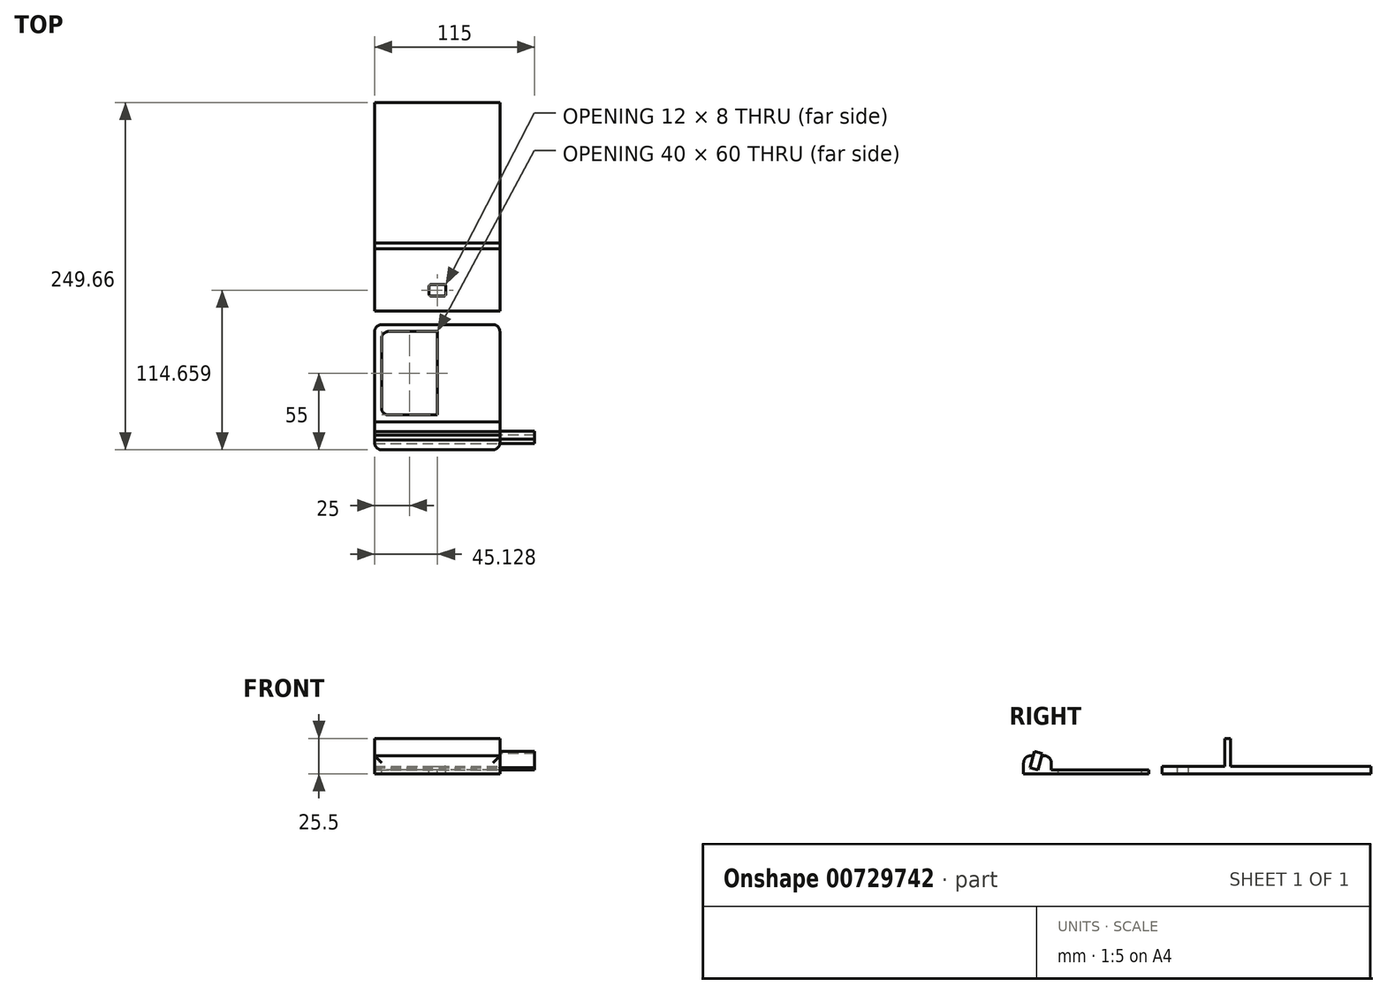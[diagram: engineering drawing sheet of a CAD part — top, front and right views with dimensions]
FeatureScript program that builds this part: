
annotation { "Feature Type Name" : "Feature", "Feature Type Description" : "" }
export const myFeature = defineFeature(function(context is Context, id is Id, definition is map)
    precondition{}
    {
        {
            var Q0;
            Q0=qCreatedBy(makeId("Top.planeOp"),FACE);
            var sketch = newSketch(context, id + "F0", { "sketchPlane" : qUnion([Q0])});
            skLineSegment(sketch, "E0.bottom", {"start": v(45, -45) * mm, "end": v(-45, -45) * mm});
            skLineSegment(sketch, "E0.top", {"start": v(45, 45) * mm, "end": v(-45, 45) * mm});
            skLineSegment(sketch, "E0.left", {"start": v(45, -45) * mm, "end": v(45, 45) * mm});
            skLineSegment(sketch, "E0.right", {"start": v(-45, -45) * mm, "end": v(-45, 45) * mm});
            skPoint(sketch, "E0.middle", {"position": v(0, 0) * mm});
            skSolve(sketch);
        }
        {
            var Q0;
            Q0 = qSketchRegion(id + "F0", true);
            extrude(context, id + "F1", {"entities" : qUnion([Q0]), "depth" : 3 * mm, "offsetDistance" : 25 * mm});
        }
        {
            var Q0;
            Q0=makeQuery(id+"F1.opExtrude","SWEPT_FACE",FACE,{"disambiguationData":[OSD([sQuery(id+"F0.wireOp",EDGE,"E0.left")])]});
            var sketch = newSketch(context, id + "F2", { "sketchPlane" : qUnion([Q0])});
            skLineSegment(sketch, "E1.bottom", {"start": v(-45, 3) * mm, "end": v(-25, 3) * mm});
            skLineSegment(sketch, "E1.top", {"start": v(-45, 13) * mm, "end": v(-25, 13) * mm});
            skLineSegment(sketch, "E1.left", {"start": v(-45, 3) * mm, "end": v(-45, 13) * mm});
            skLineSegment(sketch, "E1.right", {"start": v(-25, 3) * mm, "end": v(-25, 13) * mm});
            skSolve(sketch);
        }
        {
            var Q0;
            Q0=makeQuery(id+"F2.imprint","IMPRINT",FACE,{"disambiguationData":[TD([[makeQuery(id+"F2.imprint","IMPRINT",EDGE,{"derivedFrom":sQuery(id+"F2.wireOp",EDGE,"E1.bottom")}),1.0]])]});
            var Q1;
            Q1=makeQuery(id+"F1.opExtrude","SWEPT_FACE",FACE,{"disambiguationData":[OSD([sQuery(id+"F0.wireOp",EDGE,"E0.right")])]});
            extrude(context, id + "F3", {"entities" : qUnion([Q0]), "operationType" : NewBodyOperationType.ADD, "endBound" : BoundingType.UP_TO_SURFACE, "oppositeDirection" : true, "depth" : 25 * mm, "endBoundEntityFace" : qUnion([Q1]), "offsetDistance" : 25 * mm});
        }
        {
            var Q0;
            Q0=makeQuery(id+"F3.boolean.opBoolean","MERGE",FACE,{"derivedFrom":[makeQuery(id+"F1.opExtrude","SWEPT_FACE",FACE,{"disambiguationData":[OSD([sQuery(id+"F0.wireOp",EDGE,"E0.left")])]}),makeQuery(id+"F3.opExtrude","CAP_FACE",FACE,{"disambiguationData":[OSD([sQuery(id+"F2.wireOp",EDGE,"E1.bottom"),sQuery(id+"F2.wireOp",EDGE,"E1.top"),sQuery(id+"F2.wireOp",EDGE,"E1.left"),sQuery(id+"F2.wireOp",EDGE,"E1.right")])],"isStart":true})]});
            var sketch = newSketch(context, id + "F4", { "sketchPlane" : qUnion([Q0])});
            skLineSegment(sketch, "E2.bottom", {"start": v(-38.68, 13) * mm, "end": v(-32.68, 13) * mm});
            skLineSegment(sketch, "E2.top", {"start": v(-38.68, 1) * mm, "end": v(-32.68, 1) * mm});
            skLineSegment(sketch, "E2.left", {"start": v(-38.68, 13) * mm, "end": v(-38.68, 1) * mm});
            skLineSegment(sketch, "E2.right", {"start": v(-32.68, 13) * mm, "end": v(-32.68, 1) * mm});
            skSolve(sketch);
        }
        {
            var Q0;
            Q0=makeQuery(id+"F4.imprint","IMPRINT",FACE,{"disambiguationData":[TD([[makeQuery(id+"F4.imprint","IMPRINT",EDGE,{"derivedFrom":sQuery(id+"F4.wireOp",EDGE,"E2.bottom")}),-1.0]])]});
            var Q1;
            Q1=sQuery(id+"F4.wireOp",EDGE,"E2.bottom");
            var Q2;
            Q2=sQuery(id+"F4.wireOp",EDGE,"E2.left");
            var Q3;
            Q3=sQuery(id+"F4.wireOp",EDGE,"E2.top");
            var Q4;
            Q4=sQuery(id+"F4.wireOp",EDGE,"E2.right");
            var Q5;
            {var subQ0=sQuery(id+"F0.wireOp",EDGE,"E0.right");Q5=makeQuery(id+"F3.boolean.opBoolean","MERGE",FACE,{"derivedFrom":[makeQuery(id+"F1.opExtrude","SWEPT_FACE",FACE,{"disambiguationData":[OSD([subQ0])]}),makeQuery(id+"F3.opExtrude","CAP_FACE",FACE,{"disambiguationData":[OSD([subQ0])],"isStart":false})]});}
            extrude(context, id + "F5", {"entities" : qUnion([Q0]), "surfaceEntities" : qUnion([Q1, Q2, Q3, Q4]), "depth" : 25 * mm, "endBoundEntityFace" : qUnion([Q5]), "offsetDistance" : 25 * mm});
        }
        {
            var Q0;
            Q0=makeQuery(id+"F5.opExtrude","SWEPT_BODY",BODY,{"disambiguationData":[OSD([sQuery(id+"F4.wireOp",EDGE,"E2.bottom"),sQuery(id+"F4.wireOp",EDGE,"E2.top"),sQuery(id+"F4.wireOp",EDGE,"E2.left"),sQuery(id+"F4.wireOp",EDGE,"E2.right")])]});
            var Q1;
            Q1=makeQuery(id+"F5.opExtrude","SWEPT_EDGE",EDGE,{"disambiguationData":[OSD([sQuery(id+"F2.wireOp",EDGE,"E1.top"),sQuery(id+"F4.wireOp",EDGE,"E2.bottom"),sQuery(id+"F4.wireOp",EDGE,"E2.right")])]});
            transform(context, id + "F6", {"entities" : qUnion([Q0]), "transformType" : TransformType.ROTATION, "transformAxis" : qUnion([Q1]), "angle" : 15 * degree, "makeCopy" : false});
        }
        {
            var Q0;
            Q0=makeQuery(id+"F5.opExtrude","SWEPT_BODY",BODY,{"disambiguationData":[OSD([sQuery(id+"F4.wireOp",EDGE,"E2.bottom"),sQuery(id+"F4.wireOp",EDGE,"E2.top"),sQuery(id+"F4.wireOp",EDGE,"E2.left"),sQuery(id+"F4.wireOp",EDGE,"E2.right")])]});
            transform(context, id + "F7", {"entities" : qUnion([Q0]), "transformType" : TransformType.TRANSLATION_3D, "dx" : 0 * mm, "dy" : 1.2 * mm, "dz" : 1.5 * mm, "makeCopy" : false});
        }
        {
            var Q0;
            Q0=makeQuery(id+"F5.opExtrude","CAP_FACE",FACE,{"disambiguationData":[OSD([sQuery(id+"F4.wireOp",EDGE,"E2.bottom"),sQuery(id+"F4.wireOp",EDGE,"E2.top"),sQuery(id+"F4.wireOp",EDGE,"E2.left"),sQuery(id+"F4.wireOp",EDGE,"E2.right")])],"isStart":true});
            extrude(context, id + "F8", {"entities" : qUnion([Q0]), "operationType" : NewBodyOperationType.REMOVE, "depth" : 200 * mm, "offsetDistance" : 25 * mm});
        }
        {
            var Q0;
            Q0=makeQuery(id+"F1.opExtrude","SWEPT_EDGE",EDGE,{"disambiguationData":[OSD([sQuery(id+"F0.wireOp",EDGE,"E0.top"),sQuery(id+"F0.wireOp",EDGE,"E0.right")])]});
            var Q1;
            {var subQ0=sQuery(id+"F0.wireOp",EDGE,"E0.right");Q1=makeQuery(id+"F3.boolean.opBoolean","MERGE",EDGE,{"derivedFrom":[makeQuery(id+"F1.opExtrude","SWEPT_EDGE",EDGE,{"disambiguationData":[OSD([sQuery(id+"F0.wireOp",EDGE,"E0.bottom"),subQ0])]}),makeQuery(id+"F3.opExtrude","TWEAK_EDGE",EDGE,{"derivedFrom":[makeQuery(id+"F1.opExtrude","SWEPT_FACE",FACE,{"disambiguationData":[OSD([subQ0])]}),makeQuery(id+"F2.imprint","IMPRINT",EDGE,{"derivedFrom":sQuery(id+"F2.wireOp",EDGE,"E1.left")})]})]});}
            var Q2;
            Q2=makeQuery(id+"F3.boolean.opBoolean","MERGE",EDGE,{"derivedFrom":[makeQuery(id+"F1.opExtrude","SWEPT_EDGE",EDGE,{"disambiguationData":[OSD([sQuery(id+"F0.wireOp",EDGE,"E0.bottom"),sQuery(id+"F0.wireOp",EDGE,"E0.left")])]}),makeQuery(id+"F3.opExtrude","CAP_EDGE",EDGE,{"disambiguationData":[OSD([sQuery(id+"F2.wireOp",EDGE,"E1.left")])],"isStart":true})]});
            var Q3;
            Q3=makeQuery(id+"F3.opExtrude","SWEPT_EDGE",EDGE,{"disambiguationData":[OSD([sQuery(id+"F2.wireOp",EDGE,"E1.top"),sQuery(id+"F2.wireOp",EDGE,"E1.left")])]});
            var Q4;
            Q4=makeQuery(id+"F1.opExtrude","SWEPT_EDGE",EDGE,{"disambiguationData":[OSD([sQuery(id+"F0.wireOp",EDGE,"E0.top"),sQuery(id+"F0.wireOp",EDGE,"E0.left")])]});
            var Q5;
            Q5=makeQuery(id+"F3.opExtrude","SWEPT_EDGE",EDGE,{"disambiguationData":[OSD([sQuery(id+"F2.wireOp",EDGE,"E1.top"),sQuery(id+"F2.wireOp",EDGE,"E1.right")])]});
            fillet(context, id + "F9", {"entities" : qUnion([Q0, Q1, Q2, Q3, Q4, Q5]), "radius" : 5 * mm, "tangentPropagation" : true, "allowEdgeOverflow" : false});
        }
        {
            var Q0;
            Q0=makeQuery(id+"F1.opExtrude","CAP_FACE",FACE,{"disambiguationData":[OSD([sQuery(id+"F0.wireOp",EDGE,"E0.bottom"),sQuery(id+"F0.wireOp",EDGE,"E0.top"),sQuery(id+"F0.wireOp",EDGE,"E0.left"),sQuery(id+"F0.wireOp",EDGE,"E0.right")])],"isStart":false});
            var sketch = newSketch(context, id + "F10", { "sketchPlane" : qUnion([Q0])});
            skLineSegment(sketch, "E3.bottom", {"start": v(0, 40) * mm, "end": v(-40, 40) * mm});
            skLineSegment(sketch, "E3.top", {"start": v(0, -20) * mm, "end": v(-40, -20) * mm});
            skLineSegment(sketch, "E3.left", {"start": v(0, 40) * mm, "end": v(0, -20) * mm});
            skLineSegment(sketch, "E3.right", {"start": v(-40, 40) * mm, "end": v(-40, -20) * mm});
            skSolve(sketch);
        }
        {
            var Q0;
            Q0=makeQuery(id+"F10.imprint","IMPRINT",FACE,{"disambiguationData":[TD([[makeQuery(id+"F10.imprint","IMPRINT",EDGE,{"derivedFrom":sQuery(id+"F10.wireOp",EDGE,"E3.bottom")}),1.0]])]});
            var Q1;
            Q1=makeQuery(id+"FzDy5a0M6SfgUR9_2.1.F10.imprint","IMPRINT",FACE,{"disambiguationData":[TD([[makeQuery(id+"FzDy5a0M6SfgUR9_2.1.F10.imprint","IMPRINT",EDGE,{"derivedFrom":sQuery(id+"FzDy5a0M6SfgUR9_2.1.F10.wireOp",EDGE,"E3.bottom")}),1.0]])]});
            extrude(context, id + "F11", {"entities" : qUnion([Q0, Q1]), "operationType" : NewBodyOperationType.REMOVE, "oppositeDirection" : true, "depth" : 25 * mm, "offsetDistance" : 25 * mm});
        }
        {
            var Q0;
            Q0=makeQuery(id+"F11.boolean.opBoolean","COPY",EDGE,{"derivedFrom":makeQuery(id+"F11.opExtrude","SWEPT_EDGE",EDGE,{"disambiguationData":[OSD([sQuery(id+"F10.wireOp",EDGE,"E3.bottom"),sQuery(id+"F10.wireOp",EDGE,"E3.right")])]})});
            var Q1;
            Q1=makeQuery(id+"F11.boolean.opBoolean","COPY",EDGE,{"derivedFrom":makeQuery(id+"F11.opExtrude","SWEPT_EDGE",EDGE,{"disambiguationData":[OSD([sQuery(id+"FzDy5a0M6SfgUR9_2.1.F10.wireOp",EDGE,"E3.bottom"),sQuery(id+"FzDy5a0M6SfgUR9_2.1.F10.wireOp",EDGE,"E3.right")])]})});
            var Q2;
            Q2=makeQuery(id+"F11.boolean.opBoolean","COPY",EDGE,{"derivedFrom":makeQuery(id+"F11.opExtrude","SWEPT_EDGE",EDGE,{"disambiguationData":[OSD([sQuery(id+"FzDy5a0M6SfgUR9_2.1.F10.wireOp",EDGE,"E3.top"),sQuery(id+"FzDy5a0M6SfgUR9_2.1.F10.wireOp",EDGE,"E3.right")])]})});
            var Q3;
            Q3=makeQuery(id+"F11.boolean.opBoolean","COPY",EDGE,{"derivedFrom":makeQuery(id+"F11.opExtrude","SWEPT_EDGE",EDGE,{"disambiguationData":[OSD([sQuery(id+"F10.wireOp",EDGE,"E3.top"),sQuery(id+"F10.wireOp",EDGE,"E3.right")])]})});
            fillet(context, id + "F12", {"entities" : qUnion([Q0, Q1, Q2, Q3]), "radius" : 5 * mm, "tangentPropagation" : true, "allowEdgeOverflow" : false});
        }
        {
            var Q0;
            Q0=qCreatedBy(makeId("Top.planeOp"),FACE);
            var sketch = newSketch(context, id + "F13", { "sketchPlane" : qUnion([Q0])});
            skLineSegment(sketch, "E4.bottom", {"start": v(-44.87, 54.66) * mm, "end": v(45.13, 54.66) * mm});
            skLineSegment(sketch, "E4.top", {"start": v(-44.87, 204.66) * mm, "end": v(45.13, 204.66) * mm});
            skLineSegment(sketch, "E4.left", {"start": v(-44.87, 54.66) * mm, "end": v(-44.87, 204.66) * mm});
            skLineSegment(sketch, "E4.right", {"start": v(45.13, 54.66) * mm, "end": v(45.13, 204.66) * mm});
            skSolve(sketch);
        }
        {
            var Q0;
            Q0 = qSketchRegion(id + "F13", true);
            extrude(context, id + "F14", {"entities" : qUnion([Q0]), "depth" : 5.5 * mm, "offsetDistance" : 25 * mm});
        }
        {
            var Q0;
            Q0=makeQuery(id+"F14.opExtrude","CAP_FACE",FACE,{"disambiguationData":[OSD([sQuery(id+"F13.wireOp",EDGE,"E4.bottom"),sQuery(id+"F13.wireOp",EDGE,"E4.top"),sQuery(id+"F13.wireOp",EDGE,"E4.left"),sQuery(id+"F13.wireOp",EDGE,"E4.right")])],"isStart":false});
            var sketch = newSketch(context, id + "F15", { "sketchPlane" : qUnion([Q0])});
            skLineSegment(sketch, "E5", {"start": v(0.13, 54.66) * mm, "end": v(0.13, 99.66) * mm, "construction": true});
            skLineSegment(sketch, "E6.bottom", {"start": v(-44.87, 99.66) * mm, "end": v(45.13, 99.66) * mm});
            skLineSegment(sketch, "E6.top", {"start": v(-44.87, 103.66) * mm, "end": v(45.13, 103.66) * mm});
            skLineSegment(sketch, "E6.left", {"start": v(-44.87, 99.66) * mm, "end": v(-44.87, 103.66) * mm});
            skLineSegment(sketch, "E6.right", {"start": v(45.13, 99.66) * mm, "end": v(45.13, 103.66) * mm});
            skSolve(sketch);
        }
        {
            var Q0;
            Q0=makeQuery(id+"F15.imprint","IMPRINT",FACE,{"disambiguationData":[TD([[makeQuery(id+"F15.imprint","IMPRINT",EDGE,{"derivedFrom":sQuery(id+"F15.wireOp",EDGE,"E6.bottom")}),1.0]])]});
            extrude(context, id + "F16", {"entities" : qUnion([Q0]), "operationType" : NewBodyOperationType.ADD, "depth" : 20 * mm, "offsetDistance" : 25 * mm});
        }
        {
            var Q0;
            {var subQ0=sQuery(id+"F13.wireOp",EDGE,"E4.left");var subQ1=sQuery(id+"F13.wireOp",EDGE,"E4.right");var subQ2=sQuery(id+"F13.wireOp",EDGE,"E4.bottom");Q0=makeQuery(id+"F16.boolean.opBoolean","SPLIT",FACE,{"disambiguationData":[TD([makeQuery(id+"F14.opExtrude","SWEPT_FACE",FACE,{"disambiguationData":[OSD([subQ2])]})])],"derivedFrom":makeQuery(id+"F14.opExtrude","CAP_FACE",FACE,{"disambiguationData":[OSD([subQ2,sQuery(id+"F13.wireOp",EDGE,"E4.top"),subQ0,subQ1])],"isStart":false})});}
            var sketch = newSketch(context, id + "F17", { "sketchPlane" : qUnion([Q0])});
            skLineSegment(sketch, "E7", {"start": v(0.13, 54.66) * mm, "end": v(0.13, 69.66) * mm, "construction": true});
            skPoint(sketch, "E7.endSnap0", {"position": v(0.13, 54.66) * mm});
            skLineSegment(sketch, "E8.bottom", {"start": v(-5.87, 65.66) * mm, "end": v(6.13, 65.66) * mm});
            skLineSegment(sketch, "E8.top", {"start": v(-5.87, 73.66) * mm, "end": v(6.13, 73.66) * mm});
            skLineSegment(sketch, "E8.left", {"start": v(-5.87, 65.66) * mm, "end": v(-5.87, 73.66) * mm});
            skLineSegment(sketch, "E8.right", {"start": v(6.13, 65.66) * mm, "end": v(6.13, 73.66) * mm});
            skPoint(sketch, "E8.middle", {"position": v(0.13, 69.66) * mm});
            skLineSegment(sketch, "E9.left", {"start": v(-5.87, 73.66) * mm, "end": v(-5.87, 65.66) * mm});
            skLineSegment(sketch, "E9.right", {"start": v(6.13, 73.66) * mm, "end": v(6.13, 65.66) * mm});
            skSolve(sketch);
        }
        {
            var Q0;
            Q0 = qSketchRegion(id + "F17", true);
            extrude(context, id + "F18", {"entities" : qUnion([Q0]), "operationType" : NewBodyOperationType.REMOVE, "oppositeDirection" : true, "depth" : 25 * mm, "offsetDistance" : 25 * mm});
        }
        {
            var Q0;
            Q0=makeQuery(id+"F18.boolean.opBoolean","COPY",EDGE,{"derivedFrom":makeQuery(id+"F18.opExtrude","SWEPT_EDGE",EDGE,{"disambiguationData":[OSD([sQuery(id+"F17.wireOp",EDGE,"E8.top"),sQuery(id+"F17.wireOp",EDGE,"E9.left")])]})});
            var Q1;
            Q1=makeQuery(id+"F18.boolean.opBoolean","COPY",EDGE,{"derivedFrom":makeQuery(id+"F18.opExtrude","SWEPT_EDGE",EDGE,{"disambiguationData":[OSD([sQuery(id+"F17.wireOp",EDGE,"E8.top"),sQuery(id+"F17.wireOp",EDGE,"E9.right")])]})});
            var Q2;
            Q2=makeQuery(id+"F18.boolean.opBoolean","COPY",EDGE,{"derivedFrom":makeQuery(id+"F18.opExtrude","CAP_EDGE",EDGE,{"disambiguationData":[OSD([sQuery(id+"F17.wireOp",EDGE,"E8.bottom")])],"isStart":true})});
            var Q3;
            Q3=makeQuery(id+"F18.boolean.opBoolean","COPY",EDGE,{"derivedFrom":makeQuery(id+"F18.opExtrude","CAP_EDGE",EDGE,{"disambiguationData":[OSD([sQuery(id+"F17.wireOp",EDGE,"E9.left")])],"isStart":true})});
            var Q4;
            Q4=makeQuery(id+"F18.boolean.opBoolean","COPY",EDGE,{"derivedFrom":makeQuery(id+"F18.opExtrude","SWEPT_EDGE",EDGE,{"disambiguationData":[OSD([sQuery(id+"F17.wireOp",EDGE,"E8.bottom"),sQuery(id+"F17.wireOp",EDGE,"E9.right")])]})});
            var Q5;
            Q5=makeQuery(id+"F18.boolean.opBoolean","COPY",EDGE,{"derivedFrom":makeQuery(id+"F18.opExtrude","SWEPT_EDGE",EDGE,{"disambiguationData":[OSD([sQuery(id+"F17.wireOp",EDGE,"E8.bottom"),sQuery(id+"F17.wireOp",EDGE,"E9.left")])]})});
            fillet(context, id + "F19", {"entities" : qUnion([Q0, Q1, Q2, Q3, Q4, Q5]), "radius" : 1 * mm, "tangentPropagation" : true, "allowEdgeOverflow" : false});
        }
    });
